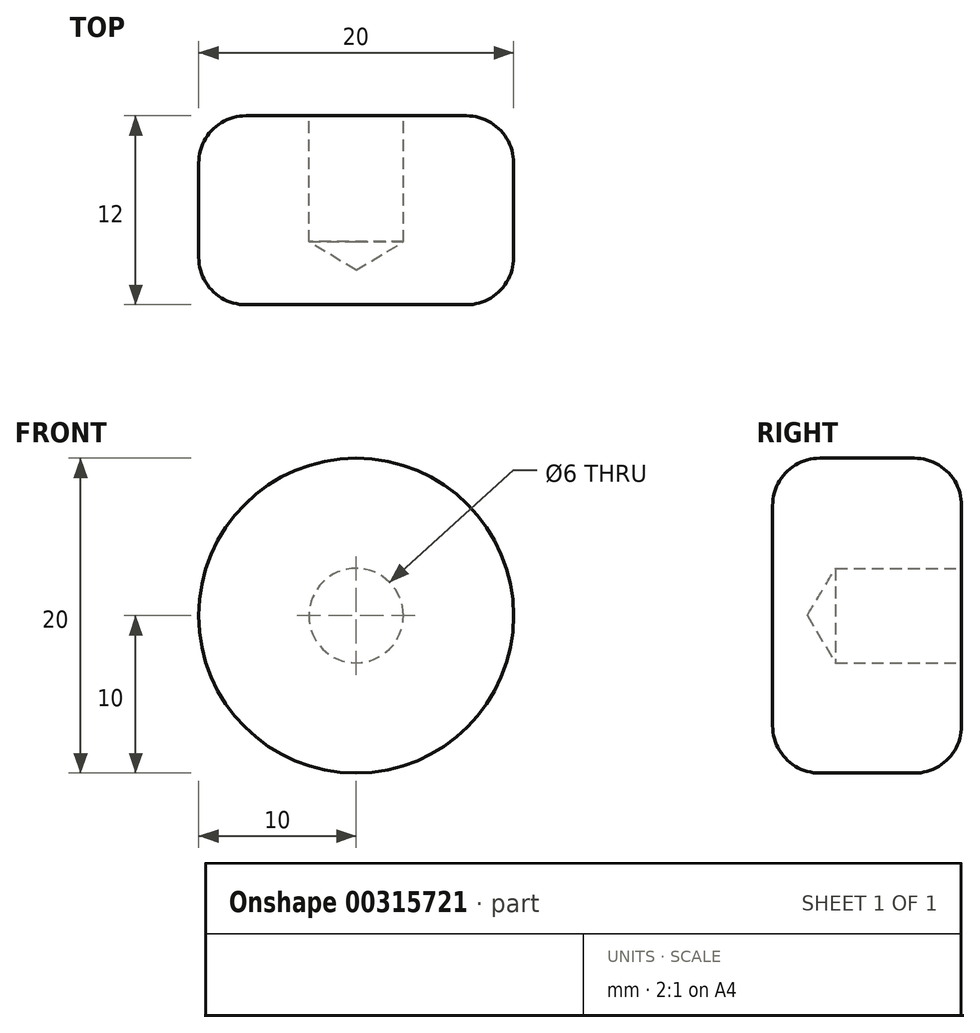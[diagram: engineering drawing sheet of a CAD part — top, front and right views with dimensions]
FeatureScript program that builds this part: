
annotation { "Feature Type Name" : "Feature", "Feature Type Description" : "" }
export const myFeature = defineFeature(function(context is Context, id is Id, definition is map)
    precondition{}
    {
        {
            var Q0;
            Q0=qCreatedBy(makeId("Front.planeOp"),FACE);
            var sketch = newSketch(context, id + "F0", { "sketchPlane" : qUnion([Q0])});
            skCircle(sketch, "E0", {"center": v(0, 0) * mm, "radius": 10 * mm});
            skSolve(sketch);
        }
        {
            var Q0;
            Q0=makeQuery(id+"F0.imprint","IMPRINT",FACE,{"disambiguationData":[TD([[makeQuery(id+"F0.imprint","IMPRINT",EDGE,{"derivedFrom":sQuery(id+"F0.wireOp",EDGE,"E0")}),1.0]])]});
            extrude(context, id + "F1", {"entities" : qUnion([Q0]), "depth" : 12 * mm});
        }
        {
            var Q0;
            Q0=makeQuery(id+"F1.opExtrude","CAP_EDGE",EDGE,{"disambiguationData":[OSD([sQuery(id+"F0.wireOp",EDGE,"E0")])],"isStart":true});
            var Q1;
            Q1=makeQuery(id+"F1.opExtrude","CAP_EDGE",EDGE,{"disambiguationData":[OSD([sQuery(id+"F0.wireOp",EDGE,"E0")])],"isStart":false});
            fillet(context, id + "F2", {"entities" : qUnion([Q0, Q1]), "radius" : 3 * mm, "tangentPropagation" : true, "allowEdgeOverflow" : false});
        }
        {
            var Q0;
            Q0=qCreatedBy(makeId("Front.planeOp"),FACE);
            var sketch = newSketch(context, id + "F3", { "sketchPlane" : qUnion([Q0])});
            skPoint(sketch, "E1", {"position": v(0, 0) * mm});
            skSolve(sketch);
        }
        {
            var Q0;
            Q0=sQuery(id+"F3.wireOp",VERTEX,"E1");
            var Q1;
            Q1=makeQuery(id+"F1.opExtrude","SWEPT_BODY",BODY,{"disambiguationData":[OSD([sQuery(id+"F0.wireOp",EDGE,"E0")])]});
            hole(context, id + "F4", {"style" : HoleStyle.SIMPLE, "endStyle" : HoleEndStyle.BLIND, "oppositeDirection" : true, "holeDiameter" : 6 * mm, "holeDepth" : 8 * mm, "tappedDepth" : 12 * mm, "tapClearance" : 3, "locations" : qUnion([Q0]), "scope" : qUnion([Q1])});
        }
    });
